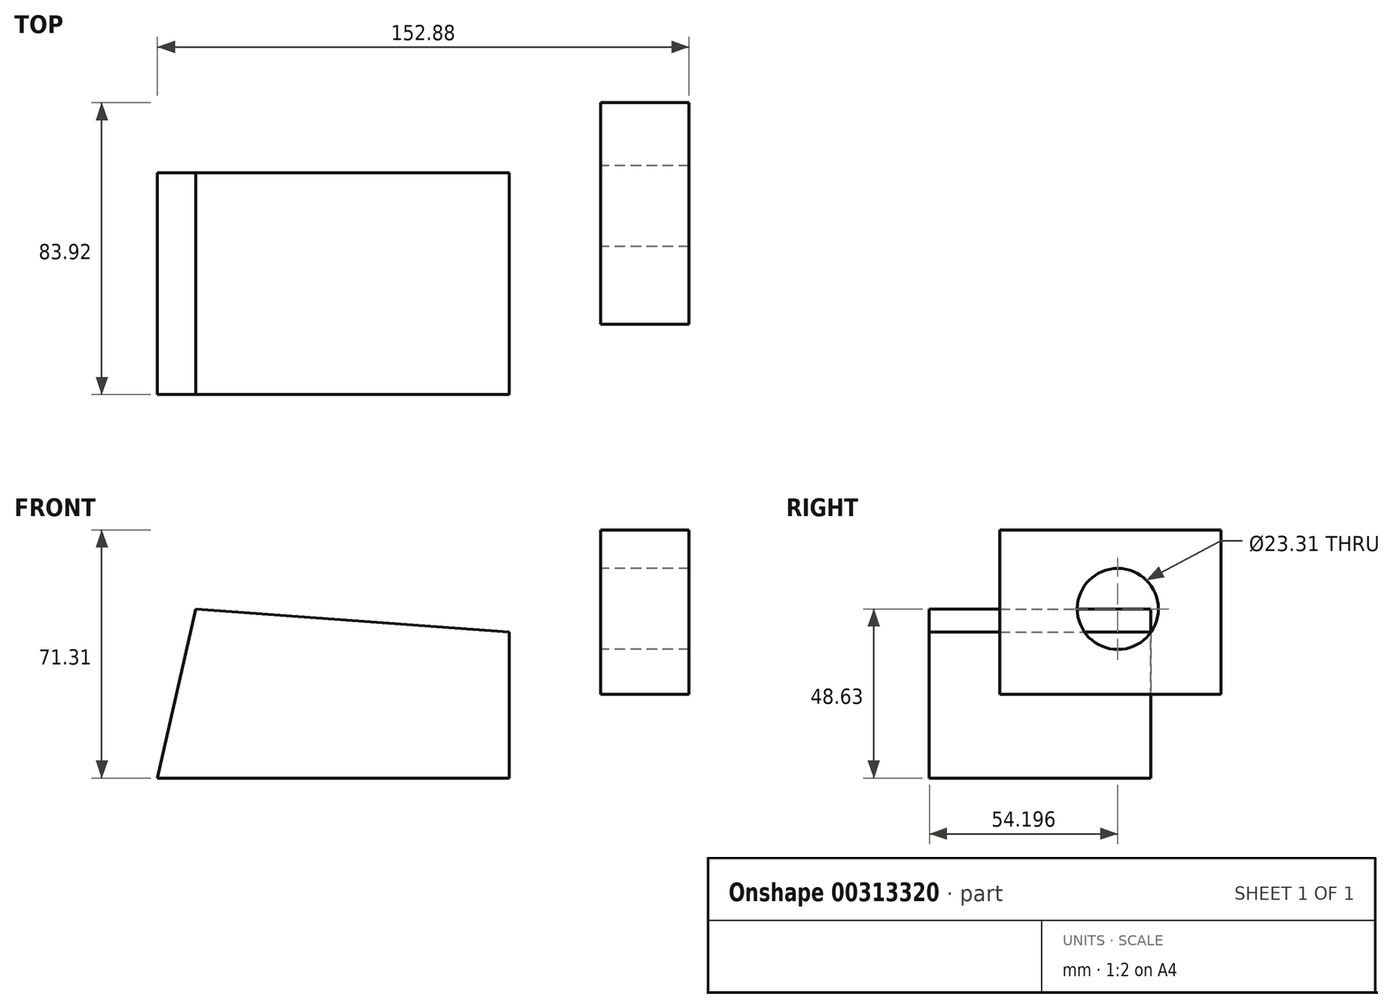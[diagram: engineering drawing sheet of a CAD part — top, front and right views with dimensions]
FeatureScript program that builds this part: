
annotation { "Feature Type Name" : "Feature", "Feature Type Description" : "" }
export const myFeature = defineFeature(function(context is Context, id is Id, definition is map)
    precondition{}
    {
        {
            var Q0;
            Q0=qCreatedBy(makeId("Right.planeOp"),FACE);
            var sketch = newSketch(context, id + "F0", { "sketchPlane" : qUnion([Q0])});
            skCircle(sketch, "E0", {"center": v(-9.55, 0) * mm, "radius": 11.65 * mm});
            skLineSegment(sketch, "E1.bottom", {"start": v(-43.52, 22.68) * mm, "end": v(20.17, 22.68) * mm});
            skLineSegment(sketch, "E1.top", {"start": v(-43.52, -24.5) * mm, "end": v(20.17, -24.5) * mm});
            skLineSegment(sketch, "E1.left", {"start": v(-43.52, 22.68) * mm, "end": v(-43.52, -24.5) * mm});
            skLineSegment(sketch, "E1.right", {"start": v(20.17, 22.68) * mm, "end": v(20.17, -24.5) * mm});
            skSolve(sketch);
        }
        {
            var Q0;
            Q0=qCreatedBy(makeId("Front.planeOp"),FACE);
            var sketch = newSketch(context, id + "F1", { "sketchPlane" : qUnion([Q0])});
            skLineSegment(sketch, "E2", {"start": v(11.03, 34.75) * mm, "end": v(-81.52, 34.75) * mm});
            skLineSegment(sketch, "E3", {"start": v(-81.52, 34.75) * mm, "end": v(-116.45, 0) * mm});
            skLineSegment(sketch, "E4", {"start": v(-116.45, 0) * mm, "end": v(-26.35, -6.7) * mm});
            skLineSegment(sketch, "E5", {"start": v(-26.35, -6.7) * mm, "end": v(-26.35, -48.63) * mm});
            skLineSegment(sketch, "E6", {"start": v(-26.35, -48.63) * mm, "end": v(-127.48, -48.63) * mm});
            skLineSegment(sketch, "E7", {"start": v(-127.48, -48.63) * mm, "end": v(-116.45, 0) * mm});
            skSolve(sketch);
        }
        {
            var Q0;
            Q0=makeQuery(id+"F0.imprint","IMPRINT",FACE,{"disambiguationData":[TD([[makeQuery(id+"F0.imprint","IMPRINT",EDGE,{"derivedFrom":sQuery(id+"F0.wireOp",EDGE,"E0")}),-1.0]])]});
            extrude(context, id + "F2", {"entities" : qUnion([Q0]), "depth" : 25.4 * mm});
        }
        {
            var Q0;
            Q0=makeQuery(id+"F1.imprint","IMPRINT",FACE,{"disambiguationData":[TD([[makeQuery(id+"F1.imprint","IMPRINT",EDGE,{"derivedFrom":sQuery(id+"F1.wireOp",EDGE,"E4")}),-1.0]])]});
            extrude(context, id + "F3", {"entities" : qUnion([Q0]), "depth" : 63.75 * mm});
        }
    });
